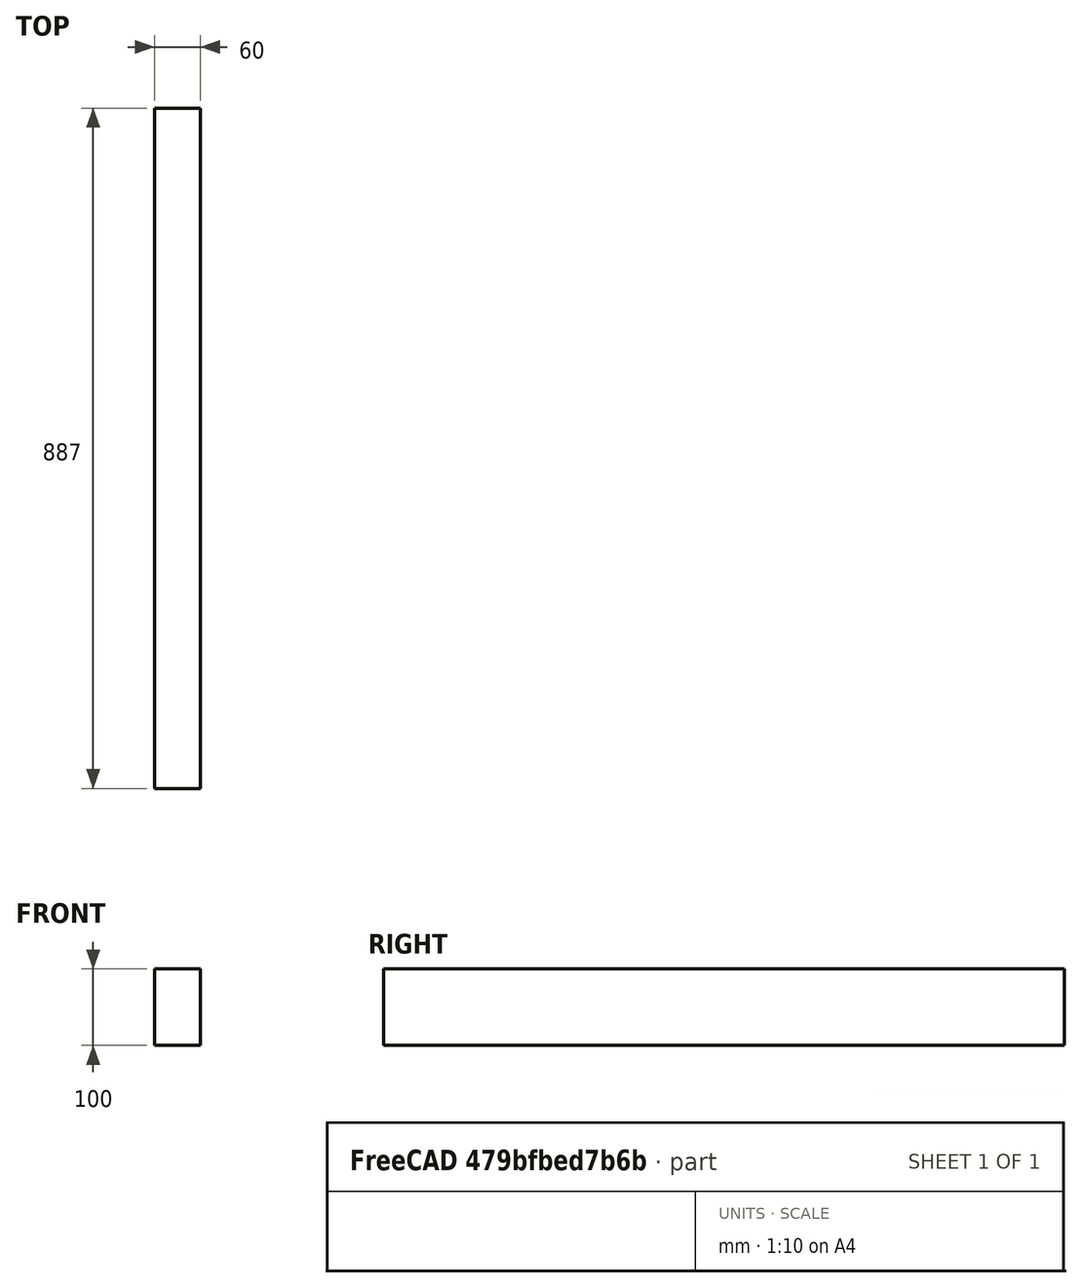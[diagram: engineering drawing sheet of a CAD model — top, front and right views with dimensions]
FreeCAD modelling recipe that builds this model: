
FCSTD DOCUMENT  (FreeCAD 1.0RUnknown)
Label: beam60x100
License: All rights reserved
LicenseURL: https://en.wikipedia.org/wiki/All_rights_reserved
objects: PartDesign::CoordinateSystem×3, Sketcher::SketchObject×1, PartDesign::Pad×1, PartDesign::Body×1, App::Part×1
note: 9 computed .brp shape members not serialized (recipe doc carries the construction recipe); baked Part::Feature solids carry a one-line shape summary decoded from their .brp

FEATURE [Sketcher::SketchObject] Sketch
  ArcFitTolerance = 1e-06
  AttachmentSupport = -> [XZ_Plane]
  FullyConstrained = true
  MakeInternals = false
  MapMode = 5
  Placement = pos=(0,0,0) rot=(1,0,0;1.5708rad)
  sketch-geometry (5):
    g0: LineSegment StartX=-30 StartY=-50 StartZ=0 EndX=30 EndY=-50 EndZ=0
    g1: LineSegment StartX=30 StartY=-50 StartZ=0 EndX=30 EndY=50 EndZ=0
    g2: LineSegment StartX=30 StartY=50 StartZ=0 EndX=-30 EndY=50 EndZ=0
    g3: LineSegment StartX=-30 StartY=50 StartZ=0 EndX=-30 EndY=-50 EndZ=0
    g4: GeomPoint [constr] X=0 Y=0 Z=0
  constraints (12):
    c: Coincident(g0,g1)
    c: Coincident(g1,g2)
    c: Coincident(g2,g3)
    c: Coincident(g3,g0)
    c: Horizontal(g0)
    c: Horizontal(g2)
    c: Vertical(g1)
    c: Vertical(g3)
    c: Symmetric(g2,g0,g4)
    c: Coincident(g4,g-1)
    c: DistanceX(g0,g0) = 60
    c: DistanceY(g3,g3) = 100
FEATURE [PartDesign::Pad] Pad
  Direction = (0,-1,2e-16)
  Length = 887
  Length2 = 10
  Midplane = true
  Placement = pos=(0,0,0) rot=(1,0,0;1.5708rad)
  Profile = -> Sketch
  ReferenceAxis = -> Sketch [N_Axis]
  Refine = true
  Suppressed = false
  Type = 0
FEATURE [PartDesign::Body] Body  label="Körper"
  AllowCompound = false
  Group = -> [Sketch,Pad]
  Origin = -> Origin
  Tip = -> Pad
FEATURE [PartDesign::CoordinateSystem] LCS_Origin
  AttacherType = Attacher::AttachEngine3D
  AttachmentSupport = -> [X_Axis001]
  MapMode = 2
FEATURE [PartDesign::CoordinateSystem] LCS_1
  AttacherType = Attacher::AttachEngine3D
  AttachmentSupport = -> [Pad]
  MapMode = 45
  Placement = pos=(-30,443.5,-1.97e-13) rot=(0,0,1;0rad)
FEATURE [PartDesign::CoordinateSystem] LCS_2
  AttacherType = Attacher::AttachEngine3D
  AttachmentSupport = -> [Pad]
  MapMode = 45
  Placement = pos=(-30,-443.5,1.97e-13) rot=(0,0,1;0rad)
FEATURE [App::Part] beam60x100x887
  Group = -> [LCS_Origin,Body,LCS_1,LCS_2]
  Origin = -> Origin001
